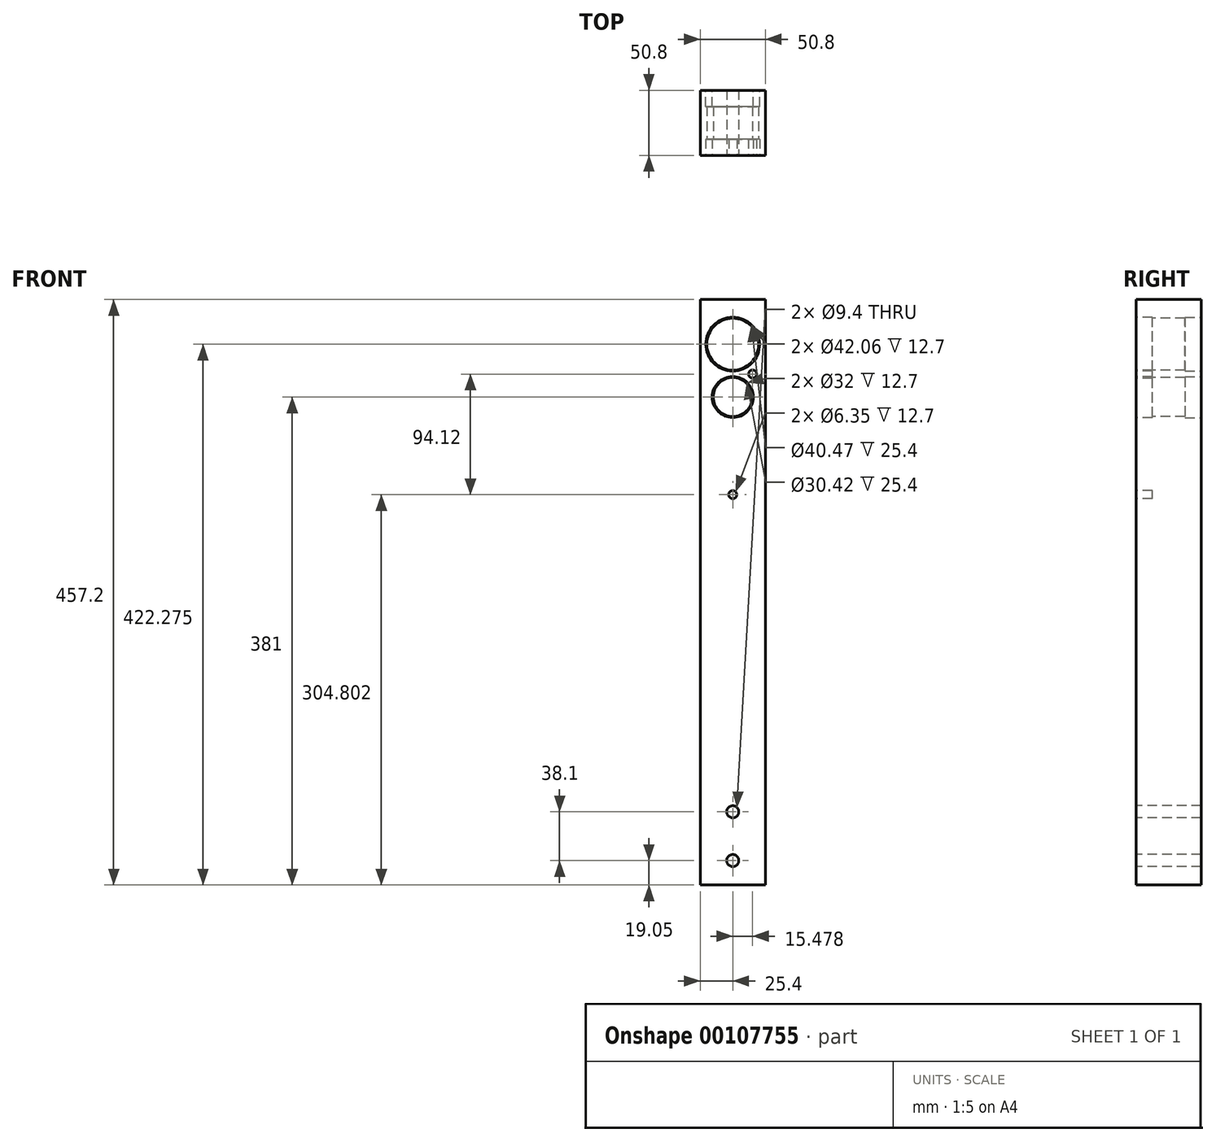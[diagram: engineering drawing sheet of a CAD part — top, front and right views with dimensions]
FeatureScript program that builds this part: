
annotation { "Feature Type Name" : "Feature", "Feature Type Description" : "" }
export const myFeature = defineFeature(function(context is Context, id is Id, definition is map)
    precondition{}
    {
        {
            var Q0;
            Q0=qCreatedBy(makeId("Front.planeOp"),FACE);
            var sketch = newSketch(context, id + "F0", { "sketchPlane" : qUnion([Q0])});
            skLineSegment(sketch, "E0.bottom", {"start": v(25.4, -228.6) * mm, "end": v(-25.4, -228.6) * mm});
            skLineSegment(sketch, "E0.top", {"start": v(25.4, 228.6) * mm, "end": v(-25.4, 228.6) * mm});
            skLineSegment(sketch, "E0.left", {"start": v(25.4, -228.6) * mm, "end": v(25.4, 228.6) * mm});
            skLineSegment(sketch, "E0.right", {"start": v(-25.4, -228.6) * mm, "end": v(-25.4, 228.6) * mm});
            skPoint(sketch, "E0.middle", {"position": v(0, 0) * mm});
            skSolve(sketch);
        }
        {
            var Q0;
            Q0 = qSketchRegion(id + "F0", true);
            extrude(context, id + "F1", {"entities" : qUnion([Q0]), "depth" : 50.8 * mm});
        }
        {
            var Q0;
            Q0=makeQuery(id+"F1.opExtrude","CAP_FACE",FACE,{"disambiguationData":[OSD([sQuery(id+"F0.wireOp",EDGE,"E0.bottom"),sQuery(id+"F0.wireOp",EDGE,"E0.top"),sQuery(id+"F0.wireOp",EDGE,"E0.left"),sQuery(id+"F0.wireOp",EDGE,"E0.right")])],"isStart":false});
            var sketch = newSketch(context, id + "F2", { "sketchPlane" : qUnion([Q0])});
            skPoint(sketch, "E1.endSnap0", {"position": v(0, -228.6) * mm});
            skCircle(sketch, "E2", {"center": v(0, -171.45) * mm, "radius": 4.7 * mm});
            skCircle(sketch, "E3", {"center": v(0, -209.55) * mm, "radius": 4.7 * mm});
            skSolve(sketch);
        }
        {
            var Q0;
            Q0 = qSketchRegion(id + "F2", true);
            extrude(context, id + "F3", {"entities" : qUnion([Q0]), "operationType" : NewBodyOperationType.REMOVE, "endBound" : BoundingType.THROUGH_ALL, "oppositeDirection" : true, "depth" : 25.4 * mm});
        }
        {
            var Q0;
            Q0=makeQuery(id+"F1.opExtrude","CAP_FACE",FACE,{"disambiguationData":[OSD([sQuery(id+"F0.wireOp",EDGE,"E0.bottom"),sQuery(id+"F0.wireOp",EDGE,"E0.top"),sQuery(id+"F0.wireOp",EDGE,"E0.left"),sQuery(id+"F0.wireOp",EDGE,"E0.right")])],"isStart":false});
            var sketch = newSketch(context, id + "F4", { "sketchPlane" : qUnion([Q0])});
            skPoint(sketch, "E4.orphan", {"position": v(0, 228.6) * mm});
            skCircle(sketch, "E5", {"center": v(0, 193.68) * mm, "radius": 20.24 * mm});
            skCircle(sketch, "E6", {"center": v(0, 152.4) * mm, "radius": 15.2 * mm});
            skLineSegment(sketch, "E7", {"start": v(0, 228.6) * mm, "end": v(0, 193.68) * mm});
            skLineSegment(sketch, "E8", {"start": v(0, 193.68) * mm, "end": v(0, 152.4) * mm});
            skSolve(sketch);
        }
        {
            var Q0;
            Q0 = qSketchRegion(id + "F4", true);
            extrude(context, id + "F5", {"entities" : qUnion([Q0]), "operationType" : NewBodyOperationType.REMOVE, "endBound" : BoundingType.THROUGH_ALL, "oppositeDirection" : true, "depth" : 25.4 * mm});
        }
        {
            var Q0;
            Q0=makeQuery(id+"F1.opExtrude","CAP_FACE",FACE,{"disambiguationData":[OSD([sQuery(id+"F0.wireOp",EDGE,"E0.bottom"),sQuery(id+"F0.wireOp",EDGE,"E0.top"),sQuery(id+"F0.wireOp",EDGE,"E0.left"),sQuery(id+"F0.wireOp",EDGE,"E0.right")])],"isStart":false});
            var sketch = newSketch(context, id + "F6", { "sketchPlane" : qUnion([Q0])});
            skCircle(sketch, "E9", {"center": v(0, 193.68) * mm, "radius": 21.03 * mm});
            skPoint(sketch, "E10.center.orphan", {"position": v(0, 152.4) * mm});
            skSolve(sketch);
        }
        {
            var Q0;
            Q0=makeQuery(id+"F1.opExtrude","CAP_FACE",FACE,{"disambiguationData":[OSD([sQuery(id+"F0.wireOp",EDGE,"E0.bottom"),sQuery(id+"F0.wireOp",EDGE,"E0.top"),sQuery(id+"F0.wireOp",EDGE,"E0.left"),sQuery(id+"F0.wireOp",EDGE,"E0.right")])],"isStart":true});
            var sketch = newSketch(context, id + "F7", { "sketchPlane" : qUnion([Q0])});
            skCircle(sketch, "E11", {"center": v(0, 193.68) * mm, "radius": 21.03 * mm});
            skSolve(sketch);
        }
        {
            var Q0;
            Q0 = qSketchRegion(id + "F7", true);
            extrude(context, id + "F8", {"entities" : qUnion([Q0]), "operationType" : NewBodyOperationType.REMOVE, "oppositeDirection" : true, "depth" : 12.7 * mm});
        }
        {
            var Q0;
            Q0=makeQuery(id+"F1.opExtrude","CAP_FACE",FACE,{"disambiguationData":[OSD([sQuery(id+"F0.wireOp",EDGE,"E0.bottom"),sQuery(id+"F0.wireOp",EDGE,"E0.top"),sQuery(id+"F0.wireOp",EDGE,"E0.left"),sQuery(id+"F0.wireOp",EDGE,"E0.right")])],"isStart":false});
            var sketch = newSketch(context, id + "F9", { "sketchPlane" : qUnion([Q0])});
            skCircle(sketch, "E12", {"center": v(0, 152.4) * mm, "radius": 16 * mm});
            skSolve(sketch);
        }
        {
            var Q0;
            Q0 = qSketchRegion(id + "F9", true);
            extrude(context, id + "F10", {"entities" : qUnion([Q0]), "operationType" : NewBodyOperationType.REMOVE, "oppositeDirection" : true, "depth" : 12.7 * mm});
        }
        {
            var Q0;
            Q0=makeQuery(id+"F1.opExtrude","CAP_FACE",FACE,{"disambiguationData":[OSD([sQuery(id+"F0.wireOp",EDGE,"E0.bottom"),sQuery(id+"F0.wireOp",EDGE,"E0.top"),sQuery(id+"F0.wireOp",EDGE,"E0.left"),sQuery(id+"F0.wireOp",EDGE,"E0.right")])],"isStart":true});
            var sketch = newSketch(context, id + "F11", { "sketchPlane" : qUnion([Q0])});
            skCircle(sketch, "E13", {"center": v(0, 152.4) * mm, "radius": 16 * mm});
            skSolve(sketch);
        }
        {
            var Q0;
            Q0 = qSketchRegion(id + "F11", true);
            extrude(context, id + "F12", {"entities" : qUnion([Q0]), "operationType" : NewBodyOperationType.REMOVE, "oppositeDirection" : true, "depth" : 12.7 * mm});
        }
        {
            var Q0;
            Q0=makeQuery(id+"F1.opExtrude","CAP_FACE",FACE,{"disambiguationData":[OSD([sQuery(id+"F0.wireOp",EDGE,"E0.bottom"),sQuery(id+"F0.wireOp",EDGE,"E0.top"),sQuery(id+"F0.wireOp",EDGE,"E0.left"),sQuery(id+"F0.wireOp",EDGE,"E0.right")])],"isStart":false});
            var sketch = newSketch(context, id + "F13", { "sketchPlane" : qUnion([Q0])});
            skCircle(sketch, "E14", {"center": v(15.48, 170.32) * mm, "radius": 3.18 * mm});
            skCircle(sketch, "E15", {"center": v(0, 76.2) * mm, "radius": 3.18 * mm});
            skPoint(sketch, "E16.orphan", {"position": v(0, 152.4) * mm});
            skSolve(sketch);
        }
        {
            var Q0;
            Q0 = qSketchRegion(id + "F13", true);
            extrude(context, id + "F14", {"entities" : qUnion([Q0]), "operationType" : NewBodyOperationType.REMOVE, "oppositeDirection" : true, "depth" : 12.7 * mm});
        }
        {
            var Q0;
            Q0 = qSketchRegion(id + "F6", true);
            extrude(context, id + "F15", {"entities" : qUnion([Q0]), "operationType" : NewBodyOperationType.REMOVE, "oppositeDirection" : true, "depth" : 12.7 * mm});
        }
        {
            var Q0;
            Q0 = qSketchRegion(id + "F6", true);
            extrude(context, id + "F16", {"entities" : qUnion([Q0]), "operationType" : NewBodyOperationType.REMOVE, "oppositeDirection" : true, "depth" : 12.7 * mm});
        }
    });
